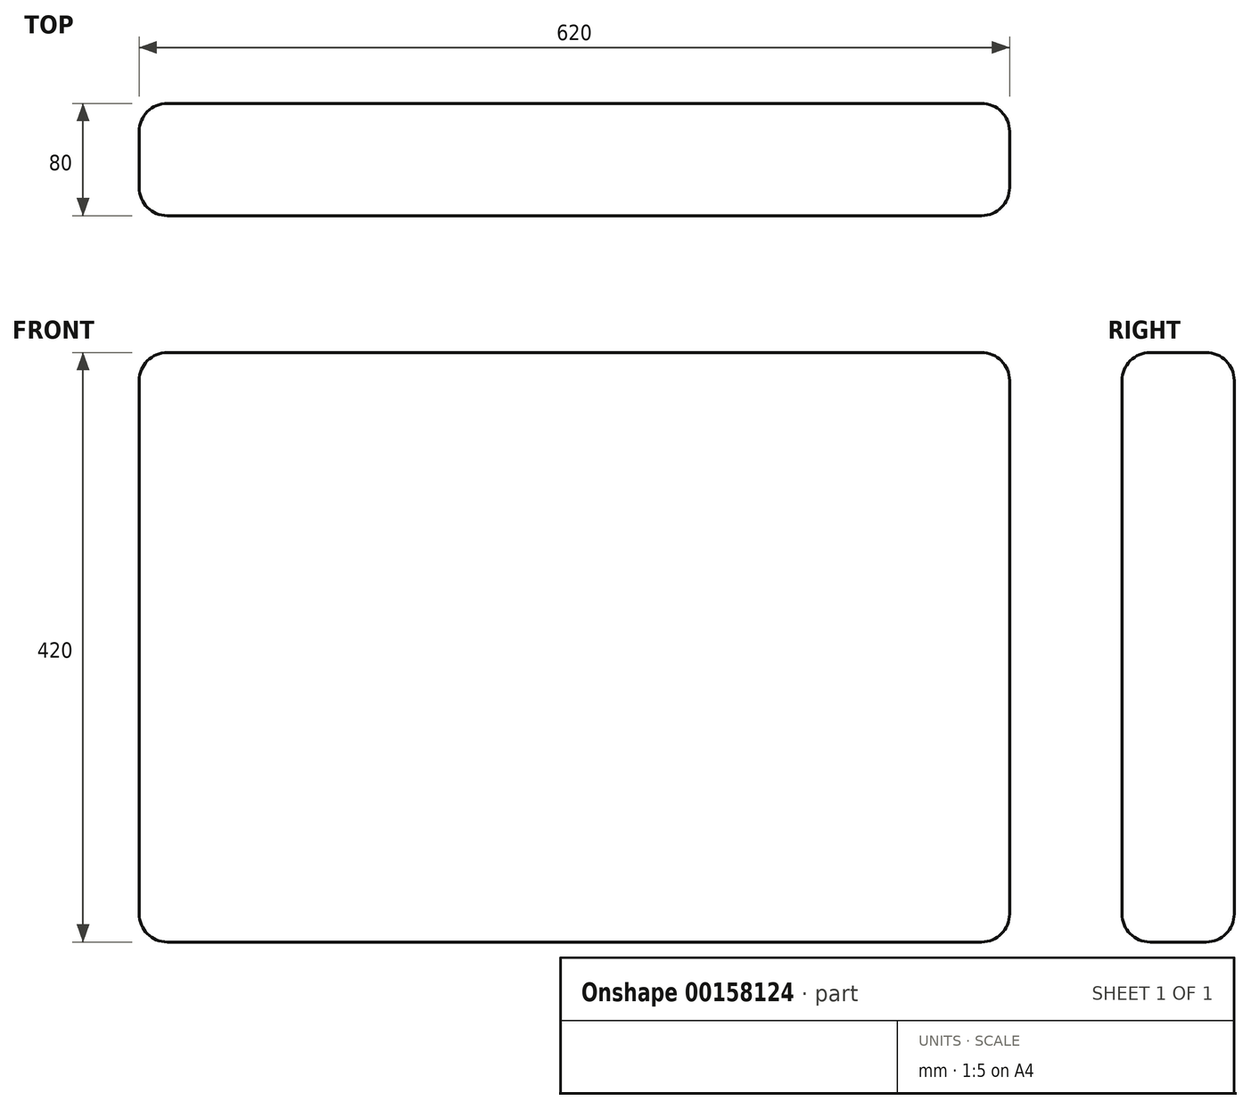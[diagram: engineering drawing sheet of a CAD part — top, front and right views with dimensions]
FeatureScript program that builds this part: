
annotation { "Feature Type Name" : "Feature", "Feature Type Description" : "" }
export const myFeature = defineFeature(function(context is Context, id is Id, definition is map)
    precondition{}
    {
        {
            var Q0;
            Q0=qCreatedBy(makeId("Front.planeOp"),FACE);
            var sketch = newSketch(context, id + "F0", { "sketchPlane" : qUnion([Q0])});
            skLineSegment(sketch, "E0.bottom", {"start": v(310, 210) * mm, "end": v(-310, 210) * mm});
            skLineSegment(sketch, "E0.top", {"start": v(310, -210) * mm, "end": v(-310, -210) * mm});
            skLineSegment(sketch, "E0.left", {"start": v(310, 210) * mm, "end": v(310, -210) * mm});
            skLineSegment(sketch, "E0.right", {"start": v(-310, 210) * mm, "end": v(-310, -210) * mm});
            skPoint(sketch, "E0.middle", {"position": v(0, 0) * mm});
            skSolve(sketch);
        }
        {
            var Q0;
            Q0=makeQuery(id+"F0.imprint","IMPRINT",FACE,{"disambiguationData":[TD([[makeQuery(id+"F0.imprint","IMPRINT",EDGE,{"derivedFrom":sQuery(id+"F0.wireOp",EDGE,"E0.bottom")}),1.0]])]});
            extrude(context, id + "F1", {"entities" : qUnion([Q0]), "endBound" : BoundingType.SYMMETRIC, "depth" : 80 * mm});
        }
        {
            var Q0;
            Q0=makeQuery(id+"F1.opExtrude","CAP_EDGE",EDGE,{"disambiguationData":[OSD([sQuery(id+"F0.wireOp",EDGE,"E0.bottom")])],"isStart":false});
            var Q1;
            Q1=makeQuery(id+"F1.opExtrude","CAP_EDGE",EDGE,{"disambiguationData":[OSD([sQuery(id+"F0.wireOp",EDGE,"E0.bottom")])],"isStart":true});
            var Q2;
            Q2=makeQuery(id+"F1.opExtrude","SWEPT_EDGE",EDGE,{"disambiguationData":[OSD([sQuery(id+"F0.wireOp",EDGE,"E0.bottom"),sQuery(id+"F0.wireOp",EDGE,"E0.right")])]});
            var Q3;
            Q3=makeQuery(id+"F1.opExtrude","SWEPT_EDGE",EDGE,{"disambiguationData":[OSD([sQuery(id+"F0.wireOp",EDGE,"E0.bottom"),sQuery(id+"F0.wireOp",EDGE,"E0.left")])]});
            var Q4;
            Q4=makeQuery(id+"F1.opExtrude","CAP_EDGE",EDGE,{"disambiguationData":[OSD([sQuery(id+"F0.wireOp",EDGE,"E0.left")])],"isStart":false});
            var Q5;
            Q5=makeQuery(id+"F1.opExtrude","CAP_EDGE",EDGE,{"disambiguationData":[OSD([sQuery(id+"F0.wireOp",EDGE,"E0.left")])],"isStart":true});
            var Q6;
            Q6=makeQuery(id+"F1.opExtrude","SWEPT_EDGE",EDGE,{"disambiguationData":[OSD([sQuery(id+"F0.wireOp",EDGE,"E0.top"),sQuery(id+"F0.wireOp",EDGE,"E0.left")])]});
            var Q7;
            Q7=makeQuery(id+"F1.opExtrude","CAP_EDGE",EDGE,{"disambiguationData":[OSD([sQuery(id+"F0.wireOp",EDGE,"E0.top")])],"isStart":false});
            var Q8;
            Q8=makeQuery(id+"F1.opExtrude","CAP_EDGE",EDGE,{"disambiguationData":[OSD([sQuery(id+"F0.wireOp",EDGE,"E0.right")])],"isStart":false});
            var Q9;
            Q9=makeQuery(id+"F1.opExtrude","CAP_EDGE",EDGE,{"disambiguationData":[OSD([sQuery(id+"F0.wireOp",EDGE,"E0.right")])],"isStart":true});
            var Q10;
            Q10=makeQuery(id+"F1.opExtrude","SWEPT_EDGE",EDGE,{"disambiguationData":[OSD([sQuery(id+"F0.wireOp",EDGE,"E0.top"),sQuery(id+"F0.wireOp",EDGE,"E0.right")])]});
            var Q11;
            Q11=makeQuery(id+"F1.opExtrude","CAP_EDGE",EDGE,{"disambiguationData":[OSD([sQuery(id+"F0.wireOp",EDGE,"E0.top")])],"isStart":true});
            fillet(context, id + "F2", {"entities" : qUnion([Q0, Q1, Q2, Q3, Q4, Q5, Q6, Q7, Q8, Q9, Q10, Q11]), "radius" : 20 * mm, "tangentPropagation" : true, "allowEdgeOverflow" : false});
        }
    });
